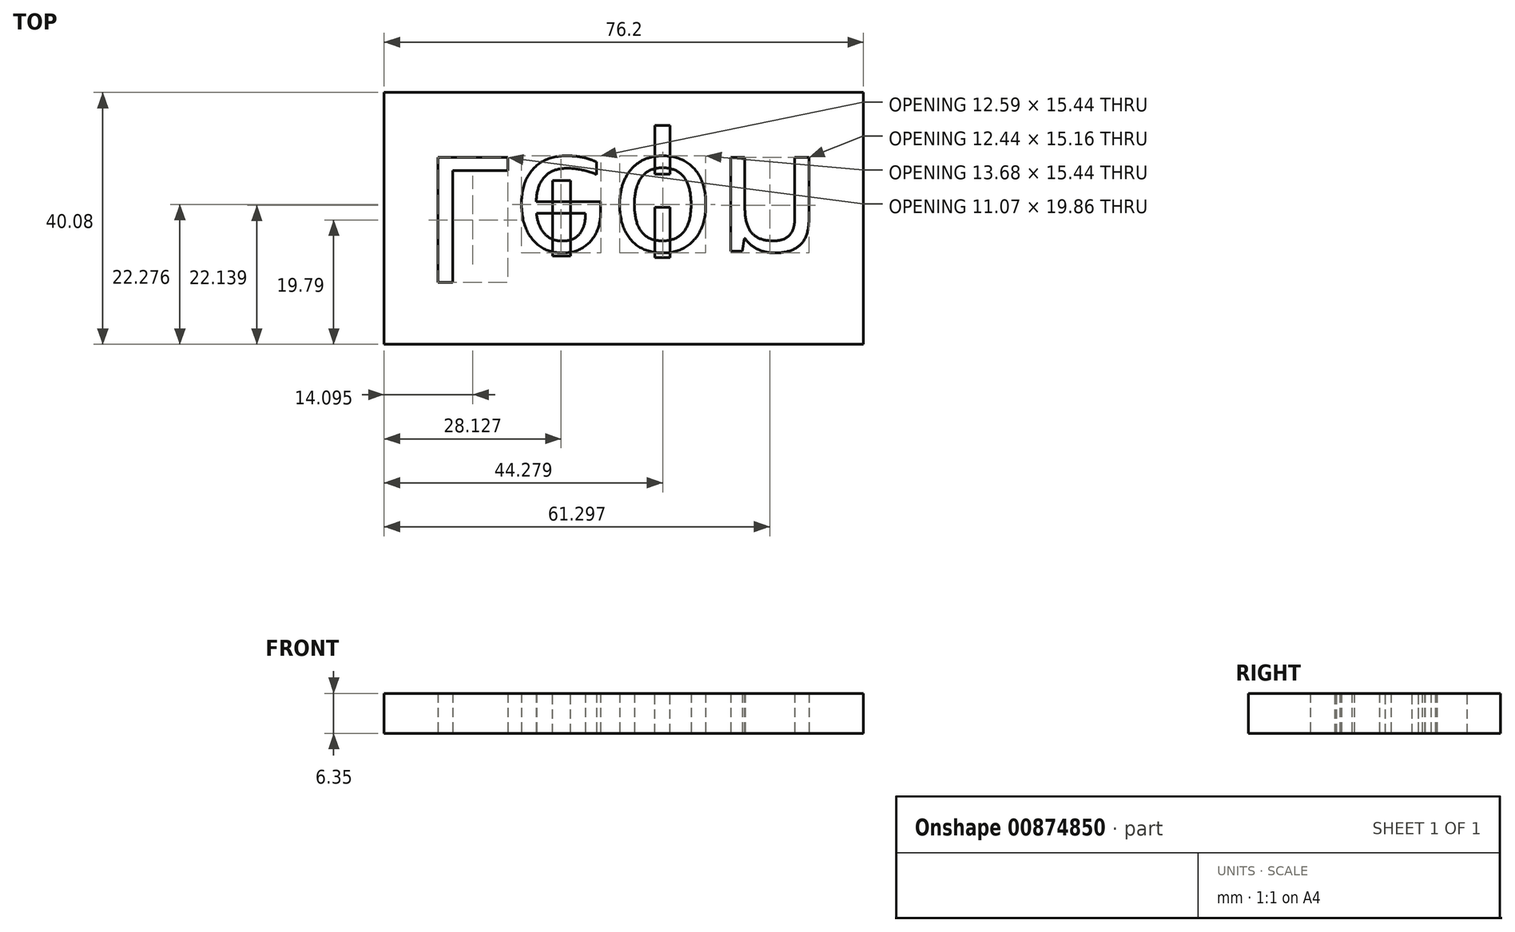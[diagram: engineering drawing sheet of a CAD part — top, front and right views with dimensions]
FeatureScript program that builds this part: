
annotation { "Feature Type Name" : "Feature", "Feature Type Description" : "" }
export const myFeature = defineFeature(function(context is Context, id is Id, definition is map)
    precondition{}
    {
        {
            var Q0;
            Q0=qCreatedBy(makeId("Top.planeOp"),FACE);
            var sketch = newSketch(context, id + "F0", { "sketchPlane" : qUnion([Q0])});
            skLineSegment(sketch, "E0.bottom", {"start": v(38.1, -20.04) * mm, "end": v(-38.1, -20.04) * mm});
            skLineSegment(sketch, "E0.top", {"start": v(38.1, 20.04) * mm, "end": v(-38.1, 20.04) * mm});
            skLineSegment(sketch, "E0.left", {"start": v(38.1, -20.04) * mm, "end": v(38.1, 20.04) * mm});
            skLineSegment(sketch, "E0.right", {"start": v(-38.1, -20.04) * mm, "end": v(-38.1, 20.04) * mm});
            skPoint(sketch, "E0.middle", {"position": v(0, 0) * mm});
            skSolve(sketch);
        }
        {
            var Q0;
            Q0=makeQuery(id+"F0.imprint","IMPRINT",FACE,{"disambiguationData":[TD([[makeQuery(id+"F0.imprint","IMPRINT",EDGE,{"derivedFrom":sQuery(id+"F0.wireOp",EDGE,"E0.bottom")}),-1.0]])]});
            extrude(context, id + "F1", {"entities" : qUnion([Q0]), "depth" : 6.35 * mm, "offsetDistance" : 25.4 * mm});
        }
        {
            var Q0;
            Q0=makeQuery(id+"F1.opExtrude","CAP_FACE",FACE,{"disambiguationData":[OSD([sQuery(id+"F0.wireOp",EDGE,"E0.bottom"),sQuery(id+"F0.wireOp",EDGE,"E0.top"),sQuery(id+"F0.wireOp",EDGE,"E0.left"),sQuery(id+"F0.wireOp",EDGE,"E0.right")])],"isStart":true});
            var sketch = newSketch(context, id + "F2", { "sketchPlane" : qUnion([Q0])});
            skText(sketch, "E1", { "text": "Leon", "fontName": "OpenSans-Regular.ttf"});
            const initialGuessF2  = {"E1": [-0.03227, -0.00968, 1, 0, 0.02003]};
            skSetInitialGuess(sketch, initialGuessF2);
            skSolve(sketch);
        }
        {
            var Q0;
            Q0 = qSketchRegion(id + "F2", true);
            extrude(context, id + "F3", {"entities" : qUnion([Q0]), "operationType" : NewBodyOperationType.REMOVE, "oppositeDirection" : true, "depth" : 48 * mm, "offsetDistance" : 25.4 * mm});
        }
        {
            var Q0;
            {var subQ0=sQuery(id+"F0.wireOp",EDGE,"E0.left");var subQ1=sQuery(id+"F0.wireOp",EDGE,"E0.bottom");var subQ2=sQuery(id+"F0.wireOp",EDGE,"E0.right");var subQ3=sQuery(id+"F0.wireOp",EDGE,"E0.top");Q0=makeQuery(id+"F3.boolean.opBoolean","SPLIT",FACE,{"disambiguationData":[TD([makeQuery(id+"F1.opExtrude","SWEPT_FACE",FACE,{"disambiguationData":[OSD([subQ1])]})])],"derivedFrom":makeQuery(id+"F1.opExtrude","CAP_FACE",FACE,{"disambiguationData":[OSD([subQ1,subQ3,subQ0,subQ2])],"isStart":false})});}
            var sketch = newSketch(context, id + "F4", { "sketchPlane" : qUnion([Q0])});
            skLineSegment(sketch, "E2.bottom", {"start": v(4.94, 7.05) * mm, "end": v(7.31, 7.05) * mm});
            skLineSegment(sketch, "E2.top", {"start": v(4.94, 14.8) * mm, "end": v(7.31, 14.8) * mm});
            skLineSegment(sketch, "E2.left", {"start": v(4.94, 7.05) * mm, "end": v(4.94, 14.8) * mm});
            skLineSegment(sketch, "E2.right", {"start": v(7.31, 7.05) * mm, "end": v(7.31, 14.8) * mm});
            skPoint(sketch, "E2.middle", {"position": v(6.13, 10.93) * mm});
            skLineSegment(sketch, "E3", {"start": v(6.13, 7.05) * mm, "end": v(6.13, -2.23) * mm});
            skLineSegment(sketch, "E4.bottom", {"start": v(4.94, 1.74) * mm, "end": v(7.31, 1.74) * mm});
            skLineSegment(sketch, "E4.top", {"start": v(4.94, -6.2) * mm, "end": v(7.31, -6.2) * mm});
            skLineSegment(sketch, "E4.left", {"start": v(4.94, 1.74) * mm, "end": v(4.94, -6.2) * mm});
            skLineSegment(sketch, "E4.right", {"start": v(7.31, 1.74) * mm, "end": v(7.31, -6.2) * mm});
            skPoint(sketch, "E4.middle", {"position": v(6.13, -2.23) * mm});
            skLineSegment(sketch, "E5.bottom", {"start": v(-11.34, 6) * mm, "end": v(-8.5, 6) * mm});
            skLineSegment(sketch, "E5.top", {"start": v(-11.34, -6) * mm, "end": v(-8.5, -6) * mm});
            skLineSegment(sketch, "E5.left", {"start": v(-11.34, 6) * mm, "end": v(-11.34, -6) * mm});
            skLineSegment(sketch, "E5.right", {"start": v(-8.5, 6) * mm, "end": v(-8.5, -6) * mm});
            skPoint(sketch, "E5.middle", {"position": v(-9.92, 0) * mm});
            skSolve(sketch);
        }
        {
            var Q0;
            {var subQ0=sQuery(id+"F4.wireOp",EDGE,"E4.left");var subQ1=sQuery(id+"F4.wireOp",EDGE,"E4.bottom");var subQ2=makeQuery(id+"F4.imprint","INTERSECT",VERTEX,{"derivedFrom":[subQ1,subQ0]});Q0=makeQuery(id+"F4.imprint","IMPRINT",FACE,{"disambiguationData":[TD([[makeQuery(id+"F4.imprint","IMPRINT",EDGE,{"disambiguationData":[TD([[subQ2,-1.0]])],"derivedFrom":subQ1}),-1.0]])]});}
            var Q1;
            {var subQ6=sQuery(id+"F4.wireOp",EDGE,"E4.top");Q1=makeQuery(id+"F4.imprint","IMPRINT",FACE,{"disambiguationData":[TD([[makeQuery(id+"F4.imprint","IMPRINT",EDGE,{"derivedFrom":subQ6}),1.0]])]});}
            var Q2;
            {var subQ1=sQuery(id+"F4.wireOp",EDGE,"E2.top");Q2=makeQuery(id+"F4.imprint","IMPRINT",FACE,{"disambiguationData":[TD([[makeQuery(id+"F4.imprint","IMPRINT",EDGE,{"derivedFrom":subQ1}),-1.0]])]});}
            var Q3;
            {var subQ0=sQuery(id+"F4.wireOp",EDGE,"E2.left");var subQ1=sQuery(id+"F4.wireOp",EDGE,"E2.bottom");var subQ2=makeQuery(id+"F4.imprint","INTERSECT",VERTEX,{"derivedFrom":[subQ1,subQ0]});Q3=makeQuery(id+"F4.imprint","IMPRINT",FACE,{"disambiguationData":[TD([[makeQuery(id+"F4.imprint","IMPRINT",EDGE,{"disambiguationData":[TD([[subQ2,-1.0]])],"derivedFrom":subQ1}),1.0]])]});}
            var Q4;
            {var subQ0=makeQuery(id+"F1.opExtrude","CAP_FACE",FACE,{"disambiguationData":[OSD([sQuery(id+"F0.wireOp",EDGE,"E0.bottom"),sQuery(id+"F0.wireOp",EDGE,"E0.top"),sQuery(id+"F0.wireOp",EDGE,"E0.left"),sQuery(id+"F0.wireOp",EDGE,"E0.right")])],"isStart":false});var subQ4=sQuery(id+"F4.wireOp",EDGE,"E5.left");var subQ7=makeQuery(id+"F3.boolean.opBoolean","INTERSECT",EDGE,{"derivedFrom":[subQ0,makeQuery(id+"F3.opExtrude","SWEPT_FACE",FACE,{"disambiguationData":[OSD([sQuery(id+"F2.wireOp",EDGE,"E1.sketch_text.stroke-13")])]})]});var subQ10=makeQuery(id+"F4.imprint","INTERSECT",VERTEX,{"derivedFrom":[subQ7,subQ4]});Q4=makeQuery(id+"F4.imprint","IMPRINT",FACE,{"disambiguationData":[TD([[makeQuery(id+"F4.imprint","IMPRINT",EDGE,{"disambiguationData":[TD([[subQ10,-1.0]])],"derivedFrom":subQ4}),1.0]])]});}
            var Q5;
            {var subQ0=sQuery(id+"F4.wireOp",EDGE,"E5.bottom");Q5=makeQuery(id+"F4.imprint","IMPRINT",FACE,{"disambiguationData":[TD([[makeQuery(id+"F4.imprint","IMPRINT",EDGE,{"derivedFrom":subQ0}),-1.0]])]});}
            var Q6;
            {var subQ7=sQuery(id+"F4.wireOp",EDGE,"E5.top");Q6=makeQuery(id+"F4.imprint","IMPRINT",FACE,{"disambiguationData":[TD([[makeQuery(id+"F4.imprint","IMPRINT",EDGE,{"derivedFrom":subQ7}),1.0]])]});}
            extrude(context, id + "F5", {"entities" : qUnion([Q0, Q1, Q2, Q3, Q4, Q5, Q6]), "oppositeDirection" : true, "depth" : 6.35 * mm, "offsetDistance" : 25.4 * mm});
        }
    });
